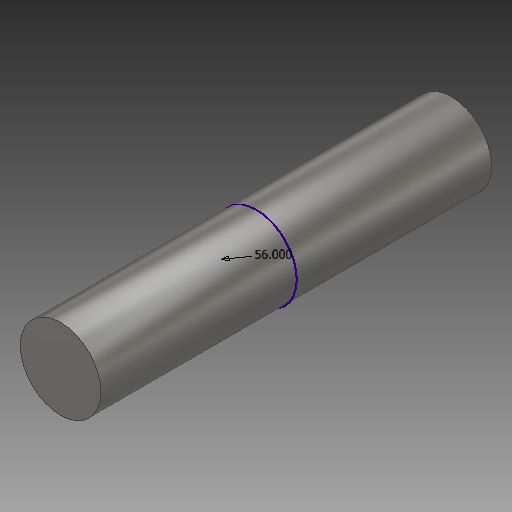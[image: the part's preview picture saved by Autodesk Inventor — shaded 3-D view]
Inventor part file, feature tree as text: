
AUTODESK INVENTOR PART (.ipt)
format: ipt  version: 2018 (Build 220112000, 112)  size: 108,032 bytes
history: native  units: in
note: dims shown in document units (in); Inventor stores cm internally (conversion verified against a paired STEP export)
features: sketch x1, extrude x1
ambient origin geometry x8: Origin, YZ Plane, XZ Plane, XY Plane, X Axis, Y Axis, Z Axis, Center Point
bodies: Solid1 (feature_tree)
feature tree (2):
  sketch  "Sketch1"  dims[d0=56.0in d1=272.0in d2=0.0in]
  extrude  "Extrusion1"  Depth=272.0in TaperAngle=0.0deg
